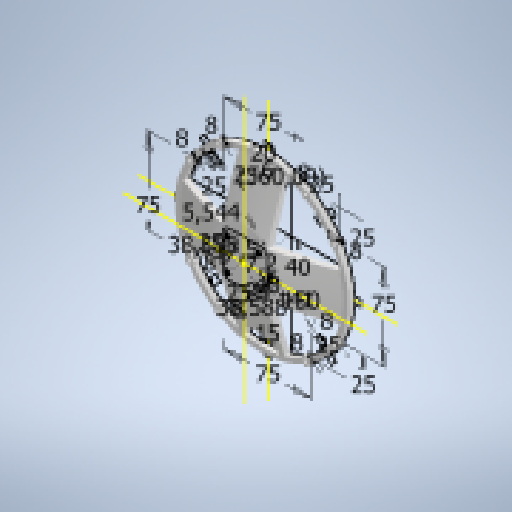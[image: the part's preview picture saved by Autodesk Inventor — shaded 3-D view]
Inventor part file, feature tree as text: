
AUTODESK INVENTOR PART (.ipt)
format: ipt  version: 2024.3 (Build 283343000, 343)  size: 350,208 bytes
history: native  units: in
note: dims shown in document units (in); Inventor stores cm internally (conversion verified against a paired STEP export)
features: sketch x4, extrude x4, chamfer x4, hole x1, revolve x1
ambient origin geometry x8: Origin, YZ Plane, XZ Plane, XY Plane, X Axis, Y Axis, Z Axis, Center Point
bodies: Solid1 (feature_tree)
feature tree (14):
  sketch  "Sketch1"  dims[d1=3.1496in d2=5.5512in d3=5.9055in d4=0.2362in d5=0.7874in d6=360.0deg d7=0.9843in d8=0.9843in d9=2.9528in d10=0.9843in d11=0.9843in d12=0.9843in d13=0.9843in d14=2.9528in d15=0.9843in d16=0.9843in d17=2.9528in d18=2.9528in d19=0.315in d20=0.315in d21=0.315in d22=0.315in d23=0.315in d24=0.315in d25=0.315in d26=0.315in d27=0.1969in d28=0.0in]
  extrude  "Extrusion1"  Depth=0.1969in TaperAngle=0.0deg
  hole  "Hole1"  [1 undecoded]
  extrude  "Extrusion2"  Depth=0.7874in TaperAngle=0.0deg
  extrude  "Extrusion3"  Depth=0.1969in
  sketch  "Sketch2"  dims[d29=0.126in d30=0.2362in d31=0.1575in d32=0.0787in d33=90.0deg d34=0.315in d35=0.8108in d36=1.5748in]
  extrude  "Extrusion4"  Depth=0.1969in
  chamfer  "Chamfer1"  Distance=0.689in
  chamfer  "Chamfer2"  Distance=0.5906in
  chamfer  "Chamfer3"  Distance=0.7874in
  chamfer  "Chamfer4"  Distance=1.6535in Angle=45.0deg
  revolve  "Revolution1"  Angle=45.0deg
  sketch  "Sketch4"  dims[d40=0.1969in d41=0.0in d42=0.1969in d43=0.1969in d44=0.689in d45=0.5906in d46=0.7874in d47=0.0in d48=1.6535in d49=0.5906in d50=45.0deg d51=1.6535in d52=0.5906in d53=45.0deg d54=1.6535in d55=0.5906in d56=45.0deg d57=1.6535in d58=0.5906in d59=45.0deg d60=2.7756in d61=360.0deg d62=0.5906in d63=0.9843in d64=1.5192in d65=1.5192in d66=0.2183in d67=0.2835in d68=0.9213in]
  sketch  "Sketch3"  dims[d37=1.5748in d38=0.7874in d39=0.0in]
note: 1 required parameter value undecoded (feature->parameter linkage not recoverable at this tier; creation-order binding heuristic only, values carry confidence <= 0.55)
